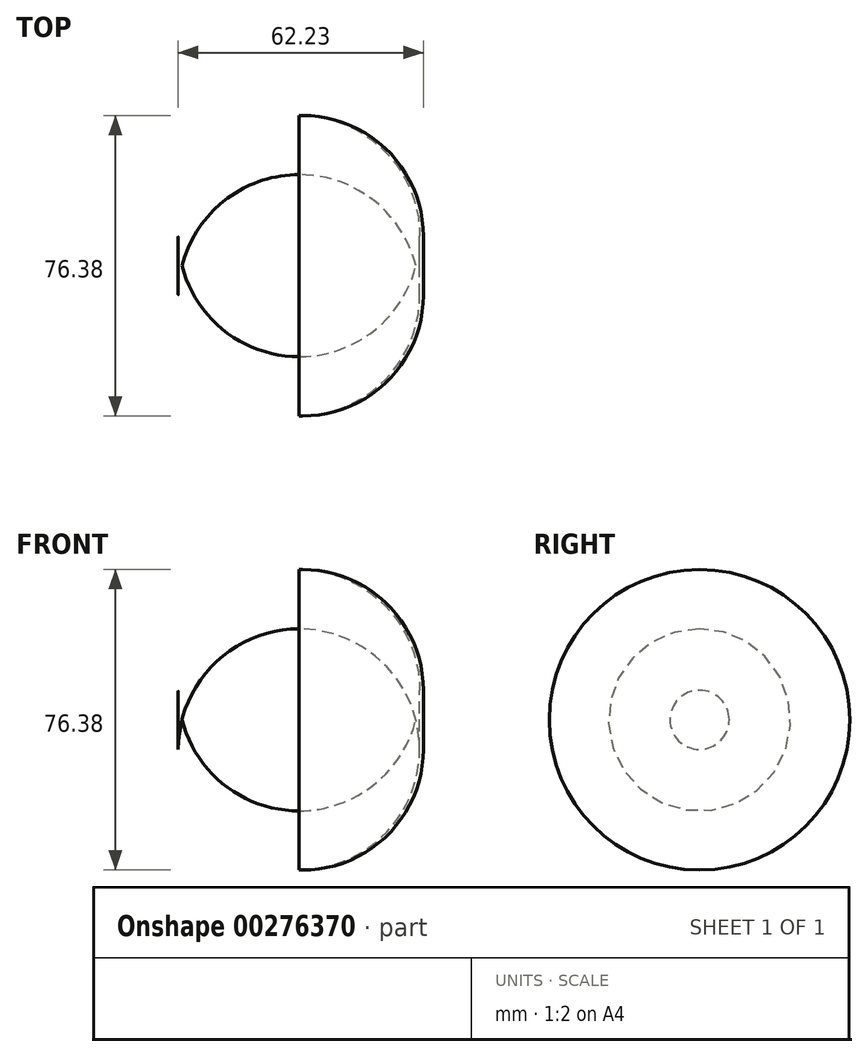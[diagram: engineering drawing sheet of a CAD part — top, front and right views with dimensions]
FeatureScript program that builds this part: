
annotation { "Feature Type Name" : "Feature", "Feature Type Description" : "" }
export const myFeature = defineFeature(function(context is Context, id is Id, definition is map)
    precondition{}
    {
        {
            var Q0;
            Q0=qCreatedBy(makeId("Right.planeOp"),FACE);
            var sketch = newSketch(context, id + "F0", { "sketchPlane" : qUnion([Q0])});
            skCircle(sketch, "E0", {"center": v(0.02, -38.19) * mm, "radius": 38.19 * mm});
            skPoint(sketch, "E0.first.point", {"position": v(0, 0) * mm});
            skPoint(sketch, "E0.second.point", {"position": v(0, -76.38) * mm});
            skPoint(sketch, "E0.third.point", {"position": v(27.75, -64.45) * mm});
            skSolve(sketch);
        }
        {
            var Q0;
            Q0=makeQuery(id+"F0.imprint","IMPRINT",FACE,{"disambiguationData":[TD([[makeQuery(id+"F0.imprint","IMPRINT",EDGE,{"derivedFrom":sQuery(id+"F0.wireOp",EDGE,"E0")}),1.0]])]});
            extrude(context, id + "F1", {"entities" : qUnion([Q0]), "depth" : 62.23 * mm});
        }
        {
            var Q0;
            Q0=makeQuery(id+"F1.opExtrude","CAP_EDGE",EDGE,{"disambiguationData":[OSD([sQuery(id+"F0.wireOp",EDGE,"E0")])],"isStart":true});
            var Q1;
            Q1=makeQuery(id+"F1.opExtrude","CAP_FACE",FACE,{"disambiguationData":[OSD([sQuery(id+"F0.wireOp",EDGE,"E0")])],"isStart":false});
            fillet(context, id + "F2", {"entities" : qUnion([Q0, Q1]), "radius" : 30.66 * mm, "tangentPropagation" : true, "allowEdgeOverflow" : false});
        }
    });
